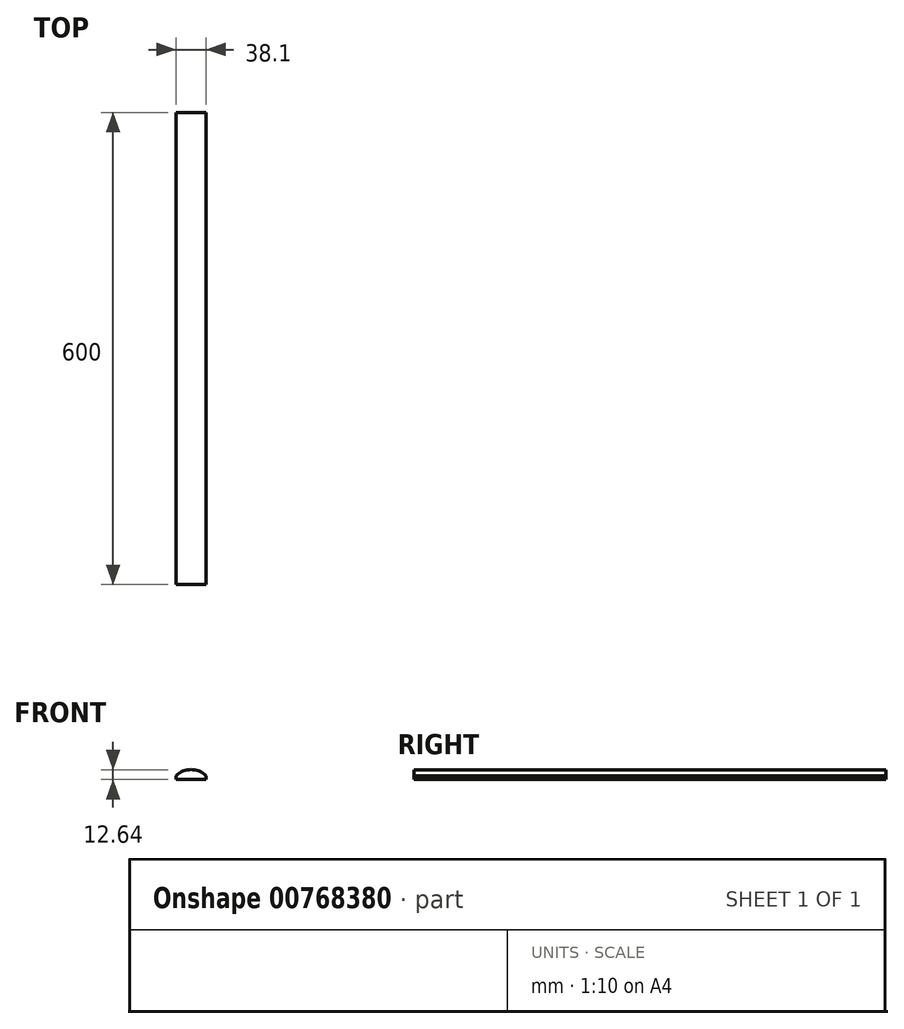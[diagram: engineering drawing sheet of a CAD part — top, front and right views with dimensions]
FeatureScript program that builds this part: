
annotation { "Feature Type Name" : "Feature", "Feature Type Description" : "" }
export const myFeature = defineFeature(function(context is Context, id is Id, definition is map)
    precondition{}
    {
        {
            var Q0;
            Q0=qCreatedBy(makeId("Front.planeOp"),FACE);
            var sketch = newSketch(context, id + "F0", { "sketchPlane" : qUnion([Q0])});
            skLineSegment(sketch, "E0.bottom", {"start": v(-21.92, 0) * mm, "end": v(16.18, 0) * mm});
            skLineSegment(sketch, "E0.top", {"start": v(-21.92, -5) * mm, "end": v(16.18, -5) * mm});
            skLineSegment(sketch, "E0.left", {"start": v(-21.92, 0) * mm, "end": v(-21.92, -5) * mm});
            skLineSegment(sketch, "E0.right", {"start": v(16.18, 0) * mm, "end": v(16.18, -5) * mm});
            skLineSegment(sketch, "E1.bottom", {"start": v(-21.92, -5) * mm, "end": v(16.18, -5) * mm, "construction": true});
            skLineSegment(sketch, "E1.top", {"start": v(-21.92, 7.7) * mm, "end": v(16.18, 7.7) * mm, "construction": true});
            skLineSegment(sketch, "E1.left", {"start": v(-21.92, -5) * mm, "end": v(-21.92, 7.7) * mm, "construction": true});
            skLineSegment(sketch, "E1.right", {"start": v(16.18, -5) * mm, "end": v(16.18, 7.7) * mm, "construction": true});
            skArc(sketch, "E2", {"start": v(16.18, 0) * mm, "mid": v(-2.87, 7.64) * mm, "end": v(-21.92, 0) * mm});
            skSolve(sketch);
        }
        {
            var Q0;
            Q0=makeQuery(id+"F0.imprint","IMPRINT",FACE,{"disambiguationData":[TD([[makeQuery(id+"F0.imprint","IMPRINT",EDGE,{"derivedFrom":sQuery(id+"F0.wireOp",EDGE,"E0.bottom")}),-1.0]])]});
            var Q1;
            Q1=makeQuery(id+"F0.imprint","IMPRINT",FACE,{"disambiguationData":[TD([[makeQuery(id+"F0.imprint","IMPRINT",EDGE,{"derivedFrom":sQuery(id+"F0.wireOp",EDGE,"E0.bottom")}),1.0]])]});
            extrude(context, id + "F1", {"entities" : qUnion([Q0, Q1]), "depth" : 600 * mm, "offsetDistance" : 25 * mm});
        }
    });
